# Revit family: ASH_Contour21_S6477_BIM_GB
name_source: partatom
category: Plumbing Fixtures
revit_build: Autodesk Revit MEP 2014 (Build: 20130308_1515(x64)
units: mm (PartAtom-declared; Revit-internal decimal feet)

## types (5) — shared parameters
AccessibilityPerformance = Doc M
Accessories = www.idealspec.co.uk
AreaUnits = millimeters
Assembly Code = C1030200
AssetType = Fixed
BREEAMApproved = No
BarCode = 0
Brand = Armitage Shanks
ConnectionType = Plumbing
DurationUnit = year
ECA = No
ExpectedLife = 30
Help = www.idealspec.co.uk/contact-us.html
IfcExportAs = IfcValveType
IfcExportType = FAUCET
InstallationInstructions = www.idealspec.co.uk/resources.html
LinearUnits = millimeters
ManufacturerURL = www.idealspec.co.uk
Material = Brass
NBSDescription = Support rails
NBSReference = 45-35-70/360
NettWeight = 2.3 Kg
NominalHeight = 35 mm
NominalLength = 92 mm
NominalWidth = 43 mm
Shape = Sculptured
Size = 35 x 92 x 43 mm
Space = Internal
SpareParts = www.fastpart-spares.co.uk
TMV3 = Yes
URL = www.idealspec.co.uk
Uniclass2015Description = Support Rails
Uniclass2015Reference = Pr_40_20_76_84
Uniclass2015Version = Products v1.1
Version = 1
VolumeUnits = Litres
WRAS = Yes
WarrantyDescription = Manufacturers Warranty
WarrantyDurationParts = 5
WarrantyDurationUnit = year
WaterEfficientProduct = No
zero-valued in all types: CWFU, Cost, Default Elevation, HWFU, WFU

## per-type parameters (varying)
| type | BIMObjectName | Color | Description | Features | Finish | FinishMtl | Model | ModelNumber | ModelReference | Name | ProductInformation |
| S647736 - Contour21 Handset Holder - Sliding - Blue | ASH_ArmitageShanks_GrabRails_Contour21_S647736 | Blue | Contour21 handset holder, sliding, blue | Handset holder, sliding, blue | Blue | ASH_ArmitageShanks_Brassware_Blue_36_Render | S647736 | S647736 | Contour21 handset holder, sliding, blue | GrabRails_Contour21_S647736_ArmitageShanks | www.idealspec.co.uk/assets/datasheet/S647736 |
| S6477AC - Contour21 Handset Holder - Sliding - White | ASH_ArmitageShanks_GrabRails_Contour21_S6477AC | White | Contour21 handset holder, sliding, white | Handset holder, sliding, white | White | ASH_ArmitageShanks_Brassware_White_AC_Render | S6477AC | S6477AC | Contour21 handset holder, sliding, white | GrabRails_Contour21_S6477AC_ArmitageShanks | www.idealspec.co.uk/assets/datasheet/S6477AC |
| S6477LJ - Contour21 Handset Holder - Sliding - Grey | ASH_ArmitageShanks_GrabRails_Contour21_S6477LJ | Grey | Contour21 handset holder, sliding, grey | Handset holder, sliding, grey | Grey | ASH_ArmitageShanks_Brassware_Grey_LJ_Render | S6477LJ | S6477LJ | Contour21 handset holder, sliding, grey | GrabRails_Contour21_S6477LJ_ArmitageShanks | www.idealspec.co.uk/assets/datasheet/S6477LJ |
| S6477RN - Contour21 Handset Holder - Sliding - Charcoal | ASH_ArmitageShanks_GrabRails_Contour21_S6477RN | Charcoal | Contour21 handset holder, sliding, charcoal | Handset holder, sliding, charcoal | Charcoal | ASH_ArmitageShanks_Brassware_Charcoal_RN_Render | S6477RN | S6477RN | Contour21 handset holder, sliding, charcoal | GrabRails_Contour21_S6477RN_ArmitageShanks | www.idealspec.co.uk/assets/datasheet/S6477RN |
| S6477MY - Contour21 Handset Holder - Sliding - Stainless Steel | ASH_ArmitageShanks_GrabRails_Contour21_S6477MY | Steel | Contour21 handset holder, sliding, stainless steel | Handset holder, sliding, stainless steel | Steel | ASH_ArmitageShanks_Brassware_Steel_MY_Render | S6477MY | S6477MY | Contour21 handset holder, sliding, stainless steel | GrabRails_Contour21_S6477MY_ArmitageShanks | www.idealspec.co.uk/assets/datasheet/S6477MY |

## geometry (parser evidence)
native form markers: Sweep x3
no freeform markers — native parametric forms only
